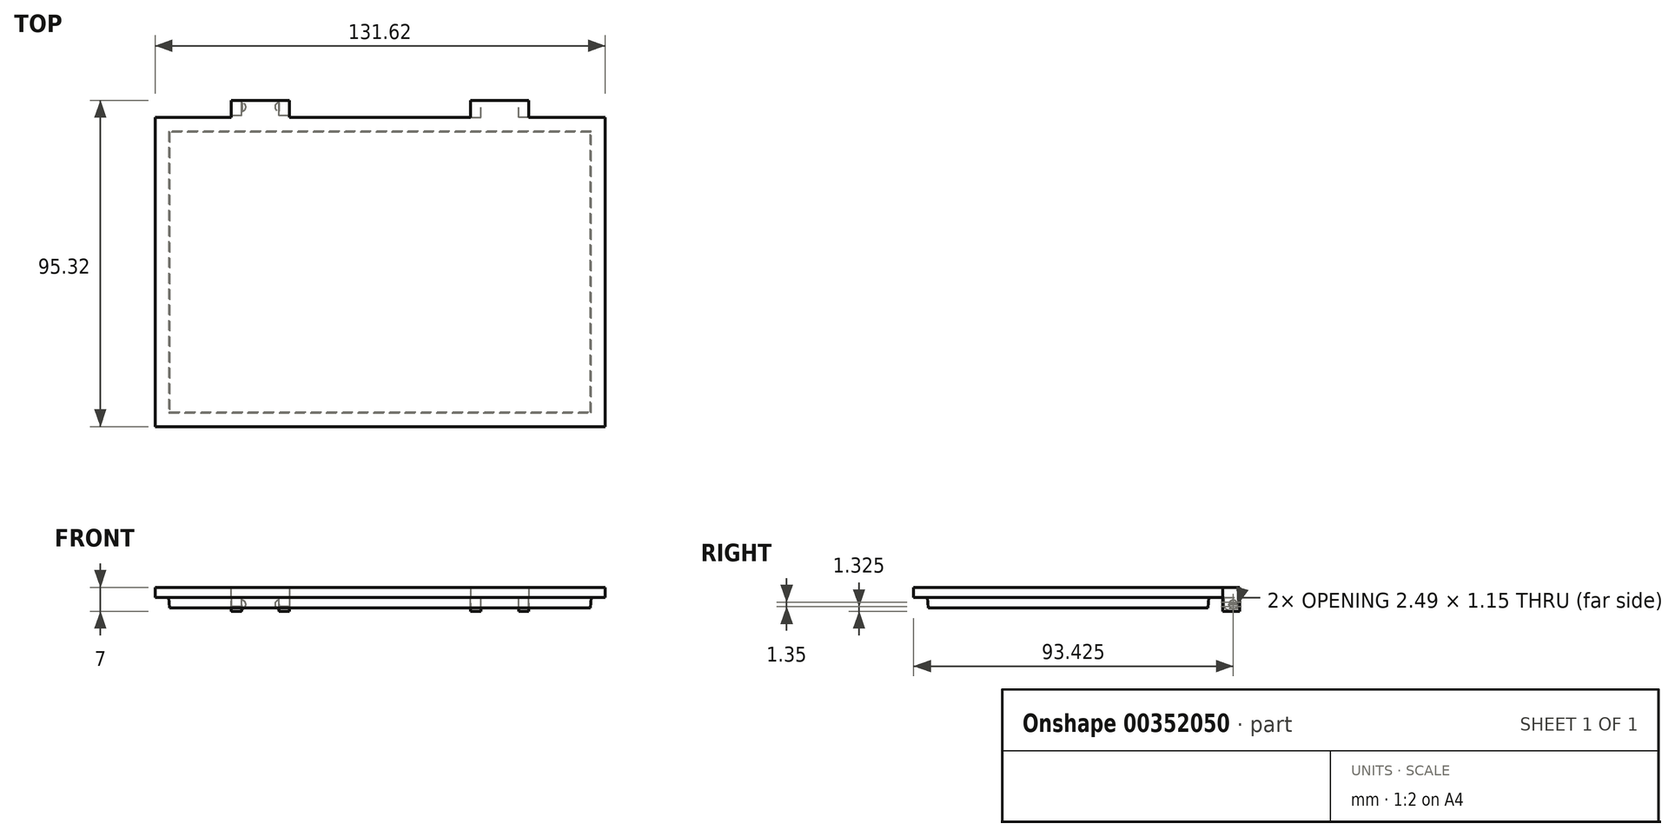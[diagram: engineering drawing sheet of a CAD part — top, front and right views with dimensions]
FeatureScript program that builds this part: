
annotation { "Feature Type Name" : "Feature", "Feature Type Description" : "" }
export const myFeature = defineFeature(function(context is Context, id is Id, definition is map)
    precondition{}
    {
        {
            var Q0;
            Q0=qCreatedBy(makeId("Top.planeOp"),FACE);
            var sketch = newSketch(context, id + "F0", { "sketchPlane" : qUnion([Q0])});
            skLineSegment(sketch, "E0.bottom", {"start": v(-65.81, 45.16) * mm, "end": v(65.81, 45.16) * mm});
            skLineSegment(sketch, "E0.top", {"start": v(-65.81, -45.16) * mm, "end": v(65.81, -45.16) * mm});
            skLineSegment(sketch, "E0.left", {"start": v(-65.81, 45.16) * mm, "end": v(-65.81, -45.16) * mm});
            skLineSegment(sketch, "E0.right", {"start": v(65.81, 45.16) * mm, "end": v(65.81, -45.16) * mm});
            skPoint(sketch, "E0.middle", {"position": v(0, 0) * mm});
            skSolve(sketch);
        }
        {
            var Q0;
            Q0 = qSketchRegion(id + "F0", true);
            extrude(context, id + "F1", {"entities" : qUnion([Q0]), "depth" : 3 * mm});
        }
        {
            var Q0;
            Q0=makeQuery(id+"F1.opExtrude","CAP_FACE",FACE,{"disambiguationData":[OSD([sQuery(id+"F0.wireOp",EDGE,"E0.bottom"),sQuery(id+"F0.wireOp",EDGE,"E0.top"),sQuery(id+"F0.wireOp",EDGE,"E0.left"),sQuery(id+"F0.wireOp",EDGE,"E0.right")])],"isStart":true});
            var sketch = newSketch(context, id + "F2", { "sketchPlane" : qUnion([Q0])});
            skLineSegment(sketch, "E1.bottom", {"start": v(-61.81, 41.16) * mm, "end": v(61.81, 41.16) * mm});
            skLineSegment(sketch, "E1.top", {"start": v(-61.81, -41.16) * mm, "end": v(61.81, -41.16) * mm});
            skLineSegment(sketch, "E1.left", {"start": v(-61.81, 41.16) * mm, "end": v(-61.81, -41.16) * mm});
            skLineSegment(sketch, "E1.right", {"start": v(61.81, 41.16) * mm, "end": v(61.81, -41.16) * mm});
            skPoint(sketch, "E1.middle", {"position": v(0, 0) * mm});
            skSolve(sketch);
        }
        {
            var Q0;
            Q0 = qSketchRegion(id + "F2", true);
            extrude(context, id + "F3", {"entities" : qUnion([Q0]), "operationType" : NewBodyOperationType.ADD, "depth" : 3 * mm, "hasDraft" : true, "draftAngle" : 5 * degree, "draftPullDirection" : true});
        }
        {
            var Q0;
            Q0=makeQuery(id+"F1.opExtrude","SWEPT_FACE",FACE,{"disambiguationData":[OSD([sQuery(id+"F0.wireOp",EDGE,"E0.bottom")])]});
            var sketch = newSketch(context, id + "F4", { "sketchPlane" : qUnion([Q0])});
            skLineSegment(sketch, "E2.bottom", {"start": v(26.5, 3) * mm, "end": v(43.5, 3) * mm});
            skLineSegment(sketch, "E2.top", {"start": v(26.5, 0) * mm, "end": v(43.5, 0) * mm});
            skLineSegment(sketch, "E2.left", {"start": v(26.5, 3) * mm, "end": v(26.5, 0) * mm});
            skLineSegment(sketch, "E2.right", {"start": v(43.5, 0) * mm, "end": v(43.5, 3) * mm});
            skLineSegment(sketch, "E3.MirrorCS", {"start": v(-26.5, 0) * mm, "end": v(-43.5, 0) * mm});
            skLineSegment(sketch, "E4.MirrorCS", {"start": v(-26.5, 3) * mm, "end": v(-43.5, 3) * mm});
            skLineSegment(sketch, "E5.MirrorCS", {"start": v(-43.5, 3) * mm, "end": v(-43.5, 0) * mm});
            skLineSegment(sketch, "E6.MirrorCS", {"start": v(-26.5, 3) * mm, "end": v(-26.5, 0) * mm});
            skSolve(sketch);
        }
        {
            var Q0;
            Q0 = qSketchRegion(id + "F4", true);
            extrude(context, id + "F5", {"entities" : qUnion([Q0]), "operationType" : NewBodyOperationType.ADD, "depth" : 5 * mm});
        }
        {
            var Q0;
            Q0=makeQuery(id+"F5.boolean.opBoolean","MERGE",FACE,{"derivedFrom":[makeQuery(id+"F1.opExtrude","CAP_FACE",FACE,{"disambiguationData":[OSD([sQuery(id+"F0.wireOp",EDGE,"E0.bottom"),sQuery(id+"F0.wireOp",EDGE,"E0.top"),sQuery(id+"F0.wireOp",EDGE,"E0.left"),sQuery(id+"F0.wireOp",EDGE,"E0.right")])],"isStart":true}),makeQuery(id+"F5.opExtrude","SWEPT_FACE",FACE,{"disambiguationData":[OSD([sQuery(id+"F4.wireOp",EDGE,"E2.top")])]}),makeQuery(id+"F5.opExtrude","SWEPT_FACE",FACE,{"disambiguationData":[OSD([sQuery(id+"F4.wireOp",EDGE,"E3.MirrorCS")])]})]});
            var sketch = newSketch(context, id + "F6", { "sketchPlane" : qUnion([Q0])});
            skLineSegment(sketch, "E7.bottom", {"start": v(-43.5, -45.16) * mm, "end": v(-26.5, -45.16) * mm, "construction": true});
            skLineSegment(sketch, "E7.top", {"start": v(-43.5, -50.16) * mm, "end": v(-26.5, -50.16) * mm, "construction": true});
            skLineSegment(sketch, "E7.left", {"start": v(-43.5, -45.16) * mm, "end": v(-43.5, -50.16) * mm, "construction": true});
            skLineSegment(sketch, "E7.right", {"start": v(-26.5, -45.16) * mm, "end": v(-26.5, -50.16) * mm, "construction": true});
            skLineSegment(sketch, "E8", {"start": v(-35, -45.16) * mm, "end": v(-35, -50.16) * mm, "construction": true});
            skLineSegment(sketch, "E9.bottom", {"start": v(-43.5, -45.16) * mm, "end": v(-40.5, -45.16) * mm});
            skLineSegment(sketch, "E9.top", {"start": v(-43.5, -50.16) * mm, "end": v(-40.5, -50.16) * mm});
            skLineSegment(sketch, "E9.left", {"start": v(-43.5, -45.16) * mm, "end": v(-43.5, -50.16) * mm});
            skLineSegment(sketch, "E9.right", {"start": v(-40.5, -45.16) * mm, "end": v(-40.5, -50.16) * mm});
            skLineSegment(sketch, "E10.MirrorCS", {"start": v(-26.5, -45.16) * mm, "end": v(-26.5, -50.16) * mm});
            skLineSegment(sketch, "E11.MirrorCS", {"start": v(-29.5, -45.16) * mm, "end": v(-29.5, -50.16) * mm});
            skLineSegment(sketch, "E12.MirrorCS", {"start": v(-26.5, -45.16) * mm, "end": v(-29.5, -45.16) * mm});
            skLineSegment(sketch, "E13.MirrorCS", {"start": v(-26.5, -50.16) * mm, "end": v(-29.5, -50.16) * mm});
            skLineSegment(sketch, "E14.MirrorCS", {"start": v(26.5, -45.16) * mm, "end": v(26.5, -50.16) * mm});
            skLineSegment(sketch, "E15.MirrorCS", {"start": v(43.5, -50.16) * mm, "end": v(40.5, -50.16) * mm});
            skLineSegment(sketch, "E16.MirrorCS", {"start": v(43.5, -45.16) * mm, "end": v(43.5, -50.16) * mm});
            skLineSegment(sketch, "E17.MirrorCS", {"start": v(26.5, -50.16) * mm, "end": v(29.5, -50.16) * mm});
            skLineSegment(sketch, "E18.MirrorCS", {"start": v(43.5, -45.16) * mm, "end": v(40.5, -45.16) * mm});
            skLineSegment(sketch, "E19.MirrorCS", {"start": v(26.5, -45.16) * mm, "end": v(26.5, -50.16) * mm, "construction": true});
            skLineSegment(sketch, "E20.MirrorCS", {"start": v(26.5, -45.16) * mm, "end": v(29.5, -45.16) * mm});
            skLineSegment(sketch, "E21.MirrorCS", {"start": v(43.5, -45.16) * mm, "end": v(43.5, -50.16) * mm, "construction": true});
            skLineSegment(sketch, "E22.MirrorCS", {"start": v(35, -45.16) * mm, "end": v(35, -50.16) * mm, "construction": true});
            skLineSegment(sketch, "E23.MirrorCS", {"start": v(43.5, -50.16) * mm, "end": v(26.5, -50.16) * mm, "construction": true});
            skLineSegment(sketch, "E24.MirrorCS", {"start": v(43.5, -45.16) * mm, "end": v(26.5, -45.16) * mm, "construction": true});
            skLineSegment(sketch, "E25.MirrorCS", {"start": v(29.5, -45.16) * mm, "end": v(29.5, -50.16) * mm});
            skLineSegment(sketch, "E26.MirrorCS", {"start": v(40.5, -45.16) * mm, "end": v(40.5, -50.16) * mm});
            skSolve(sketch);
        }
        {
            var Q0;
            Q0 = qSketchRegion(id + "F6", true);
            extrude(context, id + "F7", {"entities" : qUnion([Q0]), "operationType" : NewBodyOperationType.ADD, "depth" : 4 * mm});
        }
        {
            var Q0;
            Q0=makeQuery(id+"F7.opExtrude","CAP_EDGE",EDGE,{"disambiguationData":[OSD([sQuery(id+"F6.wireOp",EDGE,"E9.bottom")])],"isStart":false});
            var Q1;
            Q1=makeQuery(id+"F7.opExtrude","CAP_EDGE",EDGE,{"disambiguationData":[OSD([sQuery(id+"F6.wireOp",EDGE,"E12.MirrorCS")])],"isStart":false});
            fillet(context, id + "F8", {"entities" : qUnion([Q0, Q1]), "radius" : 3 * mm, "tangentPropagation" : true, "allowEdgeOverflow" : false});
        }
        {
            var Q0;
            Q0=makeQuery(id+"F7.boolean.opBoolean","MERGE",FACE,{"derivedFrom":[makeQuery(id+"F5.opExtrude","SWEPT_FACE",FACE,{"disambiguationData":[OSD([sQuery(id+"F4.wireOp",EDGE,"E2.right")])]}),makeQuery(id+"F7.opExtrude","SWEPT_FACE",FACE,{"disambiguationData":[OSD([sQuery(id+"F6.wireOp",EDGE,"E9.left")])]})]});
            var sketch = newSketch(context, id + "F9", { "sketchPlane" : qUnion([Q0])});
            skLineSegment(sketch, "E27.bottom", {"start": v(-45.16, 3) * mm, "end": v(-45.66, 3) * mm});
            skLineSegment(sketch, "E27.top", {"start": v(-45.16, -4) * mm, "end": v(-45.66, -4) * mm});
            skLineSegment(sketch, "E27.left", {"start": v(-45.16, 3) * mm, "end": v(-45.16, -4) * mm});
            skLineSegment(sketch, "E27.right", {"start": v(-45.66, 3) * mm, "end": v(-45.66, -4) * mm});
            skLineSegment(sketch, "E28", {"start": v(-45.66, 0) * mm, "end": v(-45.16, 0) * mm});
            skSolve(sketch);
        }
        {
            var Q0;
            {var subQ0=sQuery(id+"F9.wireOp",EDGE,"E28");Q0=makeQuery(id+"F9.imprint","IMPRINT",FACE,{"disambiguationData":[TD([[makeQuery(id+"F9.imprint","IMPRINT",EDGE,{"derivedFrom":subQ0}),-1.0]])]});}
            extrude(context, id + "F10", {"entities" : qUnion([Q0]), "operationType" : NewBodyOperationType.REMOVE, "oppositeDirection" : true, "depth" : 25 * mm});
        }
        {
            var Q0;
            Q0=makeQuery(id+"F7.opExtrude","SWEPT_FACE",FACE,{"disambiguationData":[OSD([sQuery(id+"F6.wireOp",EDGE,"E9.right")])]});
            var sketch = newSketch(context, id + "F11", { "sketchPlane" : qUnion([Q0])});
            skLineSegment(sketch, "E29", {"start": v(47.91, 0) * mm, "end": v(47.91, -3.99) * mm, "construction": true});
            skLineSegment(sketch, "E30", {"start": v(50.16, -2) * mm, "end": v(45.66, -2) * mm, "construction": true});
            skArc(sketch, "E31", {"start": v(49.5, -1.9) * mm, "mid": v(48.26, -0.75) * mm, "end": v(47.02, -1.9) * mm});
            skLineSegment(sketch, "E32", {"start": v(49.5, -1.9) * mm, "end": v(47.02, -1.9) * mm});
            skSolve(sketch);
        }
        {
            var Q0;
            Q0=makeQuery(id+"F11.imprint","IMPRINT",FACE,{"disambiguationData":[TD([[makeQuery(id+"F11.imprint","IMPRINT",EDGE,{"derivedFrom":sQuery(id+"F11.wireOp",EDGE,"E31")}),1.0]])]});
            var Q1;
            Q1=sQuery(id+"F11.wireOp",EDGE,"E30");
            revolve(context, id + "F12", {"operationType" : NewBodyOperationType.ADD, "entities" : qUnion([Q0]), "axis" : qUnion([Q1]), "revolveType" : RevolveType.FULL, "oppositeDirection" : true});
        }
        {
            var Q0;
            Q0=makeQuery(id+"F7.opExtrude","SWEPT_FACE",FACE,{"disambiguationData":[OSD([sQuery(id+"F6.wireOp",EDGE,"E11.MirrorCS")])]});
            var sketch = newSketch(context, id + "F13", { "sketchPlane" : qUnion([Q0])});
            skLineSegment(sketch, "E33", {"start": v(-47.91, 0) * mm, "end": v(-47.91, -3.99) * mm, "construction": true});
            skLineSegment(sketch, "E34", {"start": v(-45.66, -2) * mm, "end": v(-50.16, -2) * mm, "construction": true});
            skArc(sketch, "E35", {"start": v(-47.02, -1.9) * mm, "mid": v(-48.27, -0.75) * mm, "end": v(-49.51, -1.9) * mm});
            skLineSegment(sketch, "E36", {"start": v(-47.02, -1.9) * mm, "end": v(-49.51, -1.9) * mm});
            skPoint(sketch, "E37", {"position": v(-47.91, 0) * mm});
            skPoint(sketch, "E38", {"position": v(-50.16, -2) * mm});
            skSolve(sketch);
        }
        {
            var Q0;
            Q0=makeQuery(id+"F13.imprint","IMPRINT",FACE,{"disambiguationData":[TD([[makeQuery(id+"F13.imprint","IMPRINT",EDGE,{"derivedFrom":sQuery(id+"F13.wireOp",EDGE,"E35")}),1.0]])]});
            var Q1;
            Q1=sQuery(id+"F13.wireOp",EDGE,"E34");
            revolve(context, id + "F14", {"operationType" : NewBodyOperationType.ADD, "entities" : qUnion([Q0]), "axis" : qUnion([Q1]), "revolveType" : RevolveType.FULL});
        }
    });
